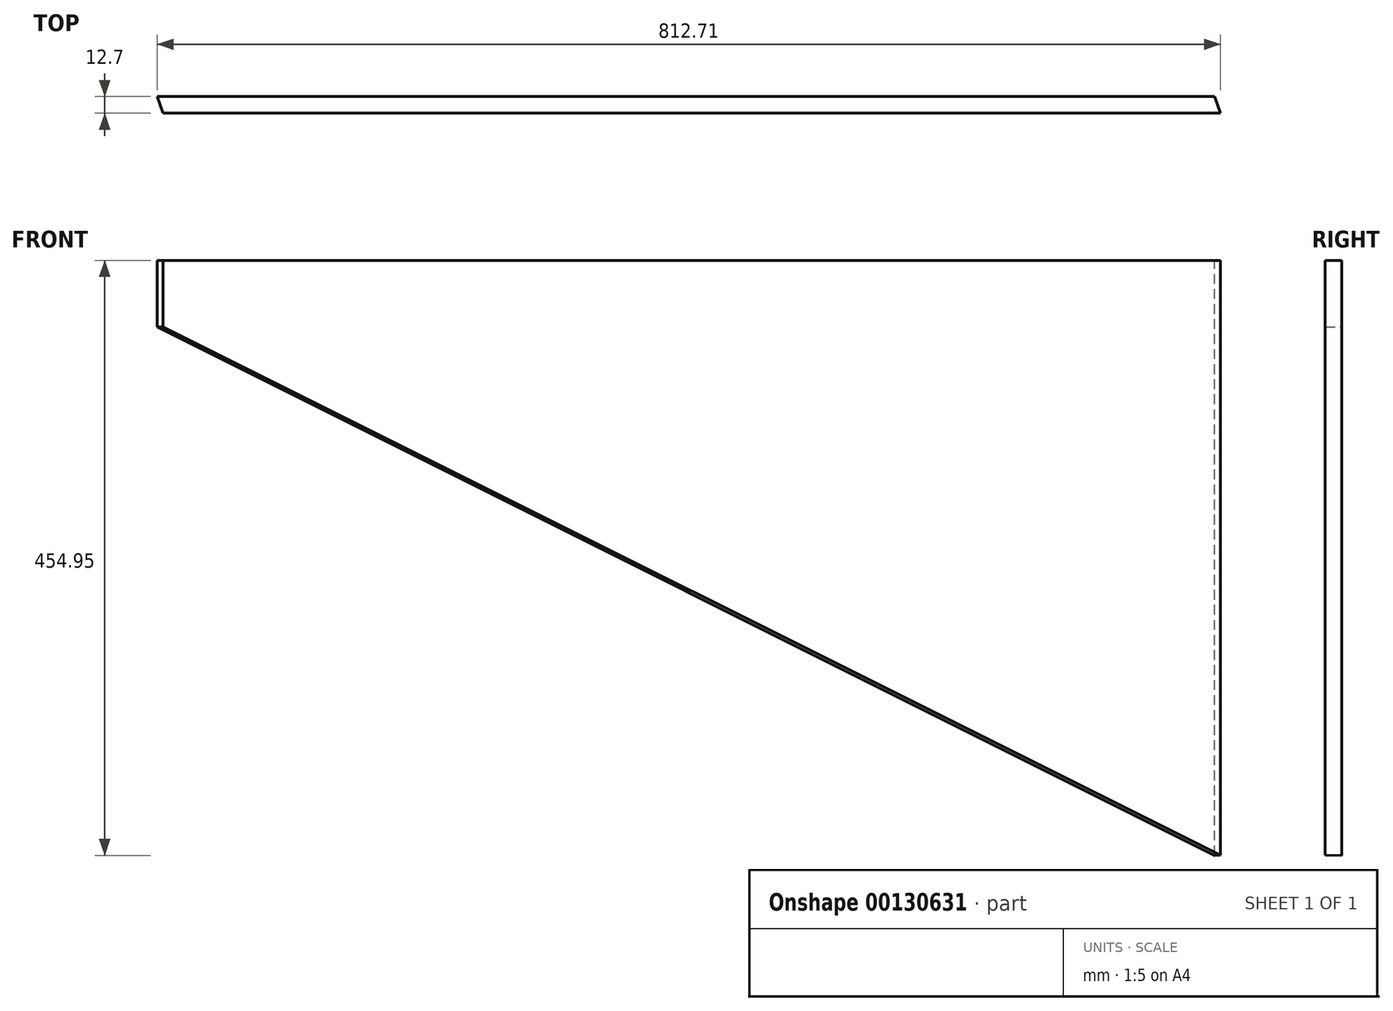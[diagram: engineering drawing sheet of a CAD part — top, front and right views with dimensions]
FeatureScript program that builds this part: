
annotation { "Feature Type Name" : "Feature", "Feature Type Description" : "" }
export const myFeature = defineFeature(function(context is Context, id is Id, definition is map)
    precondition{}
    {
        {
            var Q0;
            Q0=qCreatedBy(makeId("Front.planeOp"),FACE);
            var sketch = newSketch(context, id + "F0", { "sketchPlane" : qUnion([Q0])});
            skLineSegment(sketch, "E0", {"start": v(0, 0) * mm, "end": v(-914.4, 0) * mm});
            skLineSegment(sketch, "E1", {"start": v(-914.4, 0) * mm, "end": v(0, -457.2) * mm});
            skLineSegment(sketch, "E2", {"start": v(0, -457.2) * mm, "end": v(0, 0) * mm});
            skSolve(sketch);
        }
        {
            var Q0;
            Q0=makeQuery(id+"F0.imprint","IMPRINT",FACE,{"disambiguationData":[TD([[makeQuery(id+"F0.imprint","IMPRINT",EDGE,{"derivedFrom":sQuery(id+"F0.wireOp",EDGE,"E0")}),1.0]])]});
            extrude(context, id + "F1", {"entities" : qUnion([Q0]), "depth" : 12.7 * mm});
        }
        {
            var Q0;
            Q0=makeQuery(id+"F1.opExtrude","SWEPT_FACE",FACE,{"disambiguationData":[OSD([sQuery(id+"F0.wireOp",EDGE,"E0")])]});
            var sketch = newSketch(context, id + "F2", { "sketchPlane" : qUnion([Q0])});
            skLineSegment(sketch, "E3", {"start": v(0, -12.7) * mm, "end": v(-914.4, -12.7) * mm});
            skLineSegment(sketch, "E4", {"start": v(-914.4, -12.7) * mm, "end": v(-914.4, 287.61) * mm});
            skLineSegment(sketch, "E5", {"start": v(-914.4, 287.61) * mm, "end": v(-808.22, -12.7) * mm});
            skLineSegment(sketch, "E6", {"start": v(0, -12.7) * mm, "end": v(-125.57, 342.47) * mm});
            skLineSegment(sketch, "E7", {"start": v(-125.57, 342.47) * mm, "end": v(0, 342.47) * mm});
            skPoint(sketch, "E7.endSnap0", {"position": v(0, -6.35) * mm});
            skLineSegment(sketch, "E8", {"start": v(0, 342.47) * mm, "end": v(0, -12.7) * mm});
            skSolve(sketch);
        }
        {
            var Q0;
            Q0=makeQuery(id+"F1.opExtrude","CAP_FACE",FACE,{"disambiguationData":[OSD([sQuery(id+"F0.wireOp",EDGE,"E0"),sQuery(id+"F0.wireOp",EDGE,"E1"),sQuery(id+"F0.wireOp",EDGE,"E2")])],"isStart":false});
            var sketch = newSketch(context, id + "F3", { "sketchPlane" : qUnion([Q0])});
            skLineSegment(sketch, "E9", {"start": v(-914.4, 0) * mm, "end": v(0, -457.2) * mm});
            skLineSegment(sketch, "E10", {"start": v(-457.2, -228.6) * mm, "end": v(-251.46, 182.87) * mm});
            skLineSegment(sketch, "E11", {"start": v(-914.4, 0) * mm, "end": v(-342.9, 0) * mm});
            skSolve(sketch);
        }
        {
            var Q0;
            Q0=sQuery(id+"F3.wireOp",EDGE,"E10");
            var Q1;
            Q1=sQuery(id+"F3.wireOp",EDGE,"E9");
            cPlane(context, id + "F4", {"entities" : qUnion([Q0, Q1]), "cplaneType" : CPlaneType.LINE_ANGLE, "offset" : 25.4 * mm, "angle" : 90 * degree, "width" : 152.4 * mm, "height" : 152.4 * mm});
        }
        {
            var Q0;
            Q0=qCreatedBy(id+"F4.planeOp",FACE);
            var sketch = newSketch(context, id + "F5", { "sketchPlane" : qUnion([Q0])});
            skLineSegment(sketch, "E12", {"start": v(12.7, -153.35) * mm, "end": v(0, -153.35) * mm});
            skLineSegment(sketch, "E13", {"start": v(0, -408.93) * mm, "end": v(12.7, -406.84) * mm});
            skLineSegment(sketch, "E14", {"start": v(12.7, -406.84) * mm, "end": v(12.7, -408.93) * mm});
            skLineSegment(sketch, "E15.trimOffspring", {"start": v(12.7, -153.35) * mm, "end": v(12.7, 51.1) * mm});
            skPoint(sketch, "E16.end.orphan", {"position": v(0, -153.35) * mm});
            skPoint(sketch, "E16.start.orphan", {"position": v(0, -408.93) * mm});
            skPoint(sketch, "E17.start.orphan", {"position": v(12.7, -408.93) * mm});
            skLineSegment(sketch, "E18", {"start": v(0, -408.93) * mm, "end": v(12.7, -408.93) * mm});
            skSolve(sketch);
        }
        {
            var Q0;
            Q0=makeQuery(id+"F5.imprint","IMPRINT",FACE,{"disambiguationData":[TD([[makeQuery(id+"F5.imprint","IMPRINT",EDGE,{"derivedFrom":sQuery(id+"F5.wireOp",EDGE,"E13")}),-1.0]])]});
            extrude(context, id + "F6", {"entities" : qUnion([Q0]), "operationType" : NewBodyOperationType.REMOVE, "endBound" : BoundingType.THROUGH_ALL, "oppositeDirection" : true, "depth" : 25.4 * mm, "hasSecondDirection" : true, "secondDirectionBound" : SecondDirectionBoundingType.THROUGH_ALL, "secondDirectionOppositeDirection" : false, "secondDirectionDepth" : 25.4 * mm});
        }
        {
            var Q0;
            {var subQ0=sQuery(id+"F2.wireOp",EDGE,"E4");var subQ1=sQuery(id+"F2.wireOp",EDGE,"E3");var subQ2=makeQuery(id+"F2.imprint","INTERSECT",VERTEX,{"derivedFrom":[subQ1,subQ0]});Q0=makeQuery(id+"F2.imprint","IMPRINT",FACE,{"disambiguationData":[TD([[makeQuery(id+"F2.imprint","IMPRINT",EDGE,{"disambiguationData":[TD([[subQ2,1.0]])],"derivedFrom":subQ1}),-1.0]])]});}
            var Q1;
            {var subQ0=sQuery(id+"F2.wireOp",EDGE,"E8");var subQ3=makeQuery(id+"F1.opExtrude","CAP_EDGE",EDGE,{"disambiguationData":[OSD([sQuery(id+"F0.wireOp",EDGE,"E0")])],"isStart":true});var subQ5=makeQuery(id+"F2.imprint","INTERSECT",VERTEX,{"derivedFrom":[subQ3,subQ0]});Q1=makeQuery(id+"F2.imprint","IMPRINT",FACE,{"disambiguationData":[TD([[makeQuery(id+"F2.imprint","IMPRINT",EDGE,{"disambiguationData":[TD([[subQ5,-1.0]])],"derivedFrom":subQ3}),1.0]])]});}
            extrude(context, id + "F7", {"entities" : qUnion([Q0, Q1]), "operationType" : NewBodyOperationType.REMOVE, "endBound" : BoundingType.THROUGH_ALL, "oppositeDirection" : true, "depth" : 25.4 * mm});
        }
    });
